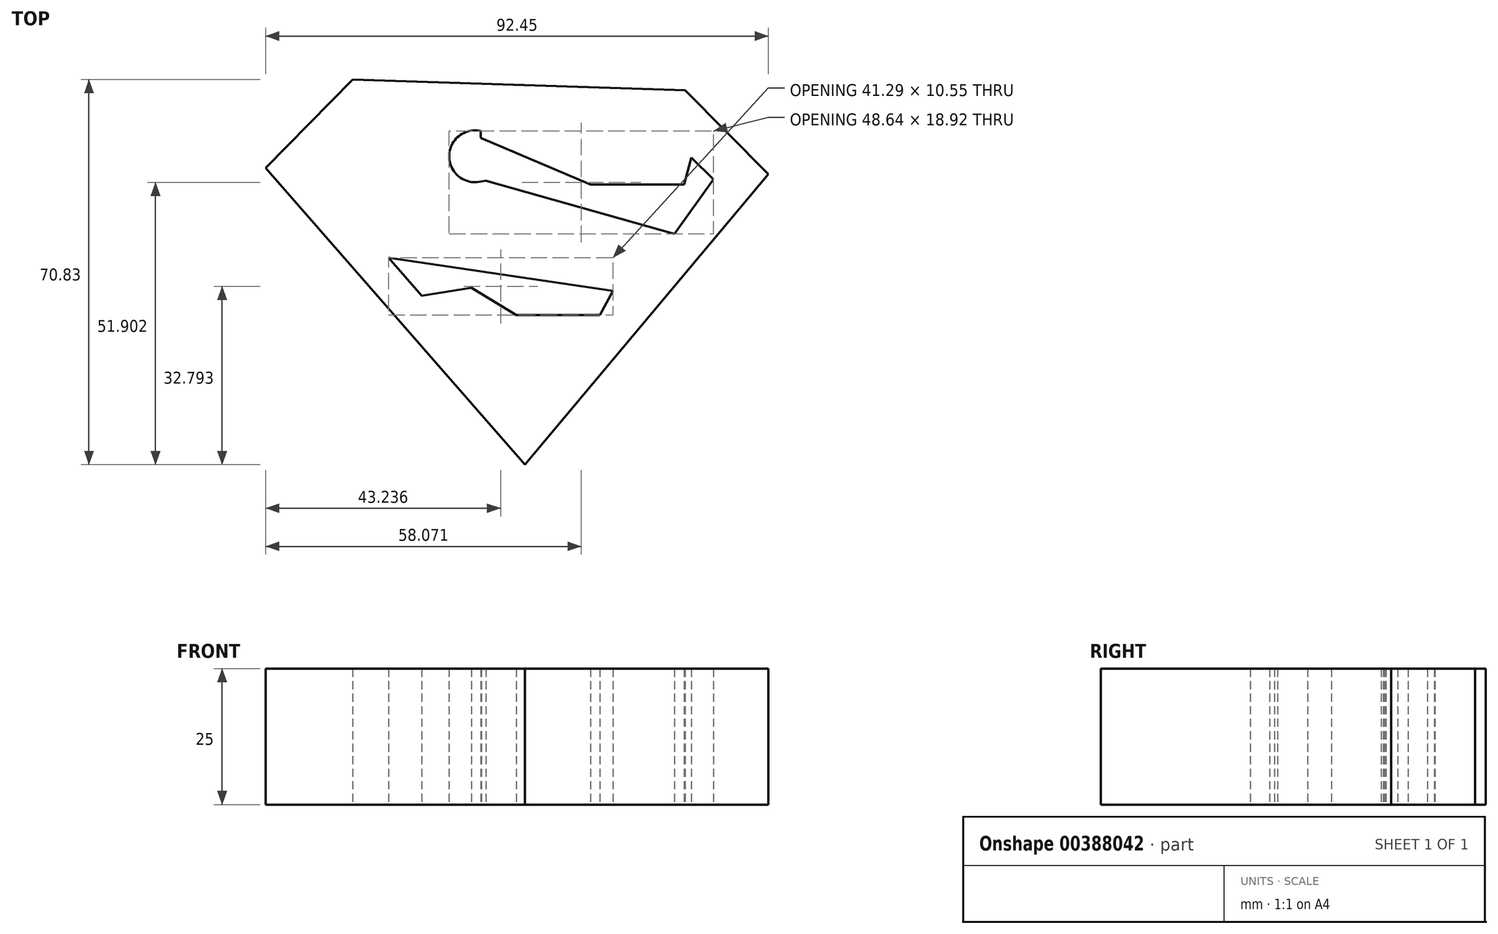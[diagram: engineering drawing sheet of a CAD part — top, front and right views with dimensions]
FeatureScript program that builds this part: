
annotation { "Feature Type Name" : "Feature", "Feature Type Description" : "" }
export const myFeature = defineFeature(function(context is Context, id is Id, definition is map)
    precondition{}
    {
        {
            var Q0;
            Q0=qCreatedBy(makeId("Top.planeOp"),FACE);
            var sketch = newSketch(context, id + "F0", { "sketchPlane" : qUnion([Q0])});
            skLineSegment(sketch, "E0", {"start": v(-28.83, 33.39) * mm, "end": v(-38.92, 23.5) * mm});
            skLineSegment(sketch, "E1", {"start": v(-38.92, 23.5) * mm, "end": v(-33.77, 16.71) * mm});
            skLineSegment(sketch, "E2", {"start": v(-33.77, 16.71) * mm, "end": v(-24.5, 33.39) * mm});
            skLineSegment(sketch, "E3", {"start": v(-28.83, 32.93) * mm, "end": v(-23.29, 33.39) * mm});
            skLineSegment(sketch, "E4", {"start": v(-25.12, 8.04) * mm, "end": v(-18.99, 1.02) * mm});
            skLineSegment(sketch, "E5", {"start": v(-18.99, 1.02) * mm, "end": v(-9.85, 2.48) * mm});
            skLineSegment(sketch, "E6", {"start": v(-9.85, 2.48) * mm, "end": v(-1.61, -2.51) * mm});
            skLineSegment(sketch, "E7", {"start": v(-1.61, -2.51) * mm, "end": v(13.74, -2.51) * mm});
            skLineSegment(sketch, "E8", {"start": v(13.74, -2.51) * mm, "end": v(16.17, 1.94) * mm});
            skLineSegment(sketch, "E9", {"start": v(16.17, 1.94) * mm, "end": v(-25.12, 8.04) * mm});
            skArc(sketch, "E10", {"start": v(-8.13, 31.33) * mm, "mid": v(-13.96, 26.64) * mm, "end": v(-8.04, 22.06) * mm});
            skLineSegment(sketch, "E11", {"start": v(-7.21, 22.2) * mm, "end": v(27.5, 12.41) * mm});
            skLineSegment(sketch, "E12", {"start": v(27.5, 12.41) * mm, "end": v(34.68, 22.44) * mm});
            skLineSegment(sketch, "E13", {"start": v(34.68, 22.44) * mm, "end": v(30.58, 26.46) * mm});
            skLineSegment(sketch, "E14", {"start": v(30.58, 26.46) * mm, "end": v(29.28, 21.52) * mm});
            skLineSegment(sketch, "E15", {"start": v(29.28, 21.52) * mm, "end": v(12.07, 21.52) * mm});
            skLineSegment(sketch, "E16", {"start": v(12.07, 21.52) * mm, "end": v(-8.13, 30.03) * mm});
            skLineSegment(sketch, "E17", {"start": v(-8.13, 30.03) * mm, "end": v(-8.13, 31.33) * mm});
            skLineSegment(sketch, "E18", {"start": v(-8.04, 22.06) * mm, "end": v(-7.21, 22.2) * mm});
            skLineSegment(sketch, "E19", {"start": v(-31.7, 40.8) * mm, "end": v(-47.7, 24.56) * mm});
            skLineSegment(sketch, "E20", {"start": v(-47.7, 24.56) * mm, "end": v(0, -30.03) * mm});
            skLineSegment(sketch, "E21", {"start": v(0, -30.03) * mm, "end": v(44.74, 23.4) * mm});
            skLineSegment(sketch, "E22", {"start": v(44.74, 23.4) * mm, "end": v(29.45, 38.83) * mm});
            skLineSegment(sketch, "E23", {"start": v(29.45, 38.83) * mm, "end": v(-31.7, 40.8) * mm});
            skSolve(sketch);
        }
        {
            var Q0;
            Q0 = qSketchRegion(id + "F0", true);
            extrude(context, id + "F1", {"entities" : qUnion([Q0]), "depth" : 25 * mm});
        }
    });
